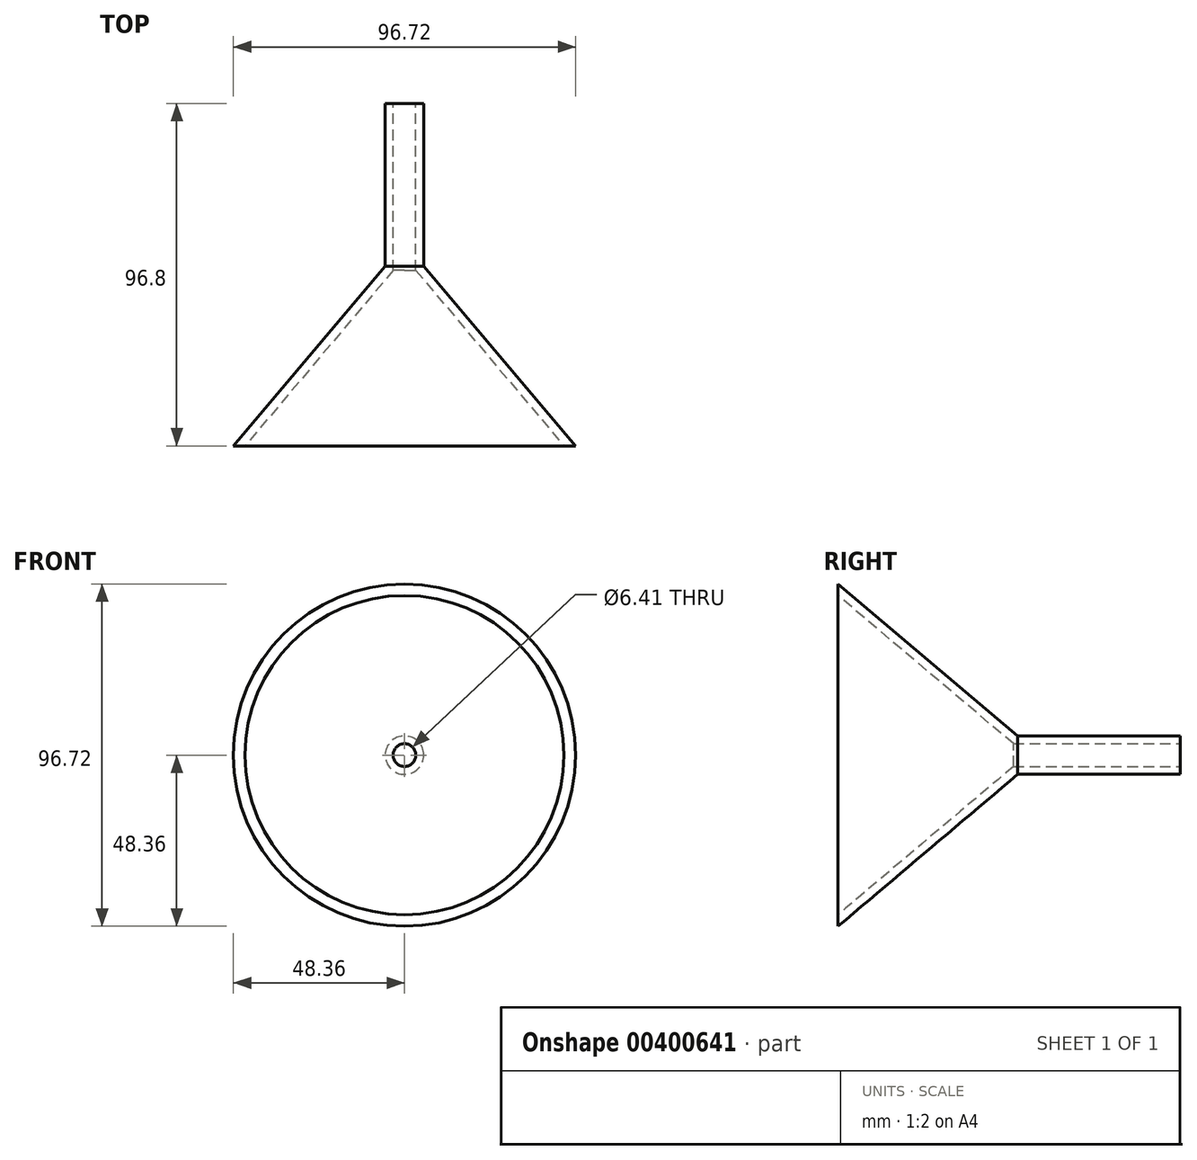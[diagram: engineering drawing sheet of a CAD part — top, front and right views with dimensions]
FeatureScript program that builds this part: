
annotation { "Feature Type Name" : "Feature", "Feature Type Description" : "" }
export const myFeature = defineFeature(function(context is Context, id is Id, definition is map)
    precondition{}
    {
        {
            var Q0;
            Q0=qCreatedBy(makeId("Front.planeOp"),FACE);
            var sketch = newSketch(context, id + "F0", { "sketchPlane" : qUnion([Q0])});
            skCircle(sketch, "E0", {"center": v(0, 0) * mm, "radius": 5.44 * mm});
            skSolve(sketch);
        }
        {
            var Q0;
            Q0 = qSketchRegion(id + "F0", true);
            extrude(context, id + "F1", {"entities" : qUnion([Q0]), "oppositeDirection" : true, "depth" : 46 * mm});
        }
        {
            var Q0;
            Q0=qCreatedBy(makeId("Front.planeOp"),FACE);
            cPlane(context, id + "F2", {"entities" : qUnion([Q0]), "cplaneType" : CPlaneType.OFFSET, "offset" : 50.8 * mm, "width" : 150 * mm, "height" : 150 * mm});
        }
        {
            var Q0;
            Q0=qCreatedBy(id+"F2.planeOp",FACE);
            var sketch = newSketch(context, id + "F3", { "sketchPlane" : qUnion([Q0])});
            skCircle(sketch, "E1", {"center": v(0, 0) * mm, "radius": 48.36 * mm});
            skSolve(sketch);
        }
        {
            var Q1;
            Q1=makeQuery(id+"F3.imprint","IMPRINT",FACE,{"disambiguationData":[TD([[makeQuery(id+"F3.imprint","IMPRINT",EDGE,{"derivedFrom":sQuery(id+"F3.wireOp",EDGE,"E1")}),1.0]])]});
            var Q2;
            Q2=makeQuery(id+"F1.opExtrude","CAP_FACE",FACE,{"disambiguationData":[OSD([sQuery(id+"F0.wireOp",EDGE,"E0")])],"isStart":true});
            loft(context, id + "F4", {"operationType" : NewBodyOperationType.ADD, "sheetProfilesArray" : [{ "sheetProfileEntities" : qUnion([Q1]) }, { "sheetProfileEntities" : qUnion([Q2]) }]});
        }
        {
            var Q0;
            Q0=makeQuery(id+"F4.opLoft","CAP_FACE",FACE,{"disambiguationData":[OSD([makeQuery(id+"F3.imprint","IMPRINT",FACE,{"disambiguationData":[TD([[makeQuery(id+"F3.imprint","IMPRINT",EDGE,{"derivedFrom":sQuery(id+"F3.wireOp",EDGE,"E1")}),1.0]])]})])],"isStart":true});
            shell(context, id + "F5", {"entities" : qUnion([Q0]), "thickness" : 2.5 * mm});
        }
        {
            var Q0;
            Q0=makeQuery(id+"F1.opExtrude","CAP_FACE",FACE,{"disambiguationData":[OSD([sQuery(id+"F0.wireOp",EDGE,"E0")])],"isStart":false});
            var sketch = newSketch(context, id + "F6", { "sketchPlane" : qUnion([Q0])});
            skCircle(sketch, "E2", {"center": v(0, 0) * mm, "radius": 3.2 * mm});
            skSolve(sketch);
        }
        {
            var Q0;
            Q0 = qSketchRegion(id + "F6", true);
            extrude(context, id + "F7", {"entities" : qUnion([Q0]), "operationType" : NewBodyOperationType.REMOVE, "endBound" : BoundingType.THROUGH_ALL, "oppositeDirection" : true, "depth" : 25 * mm});
        }
    });
